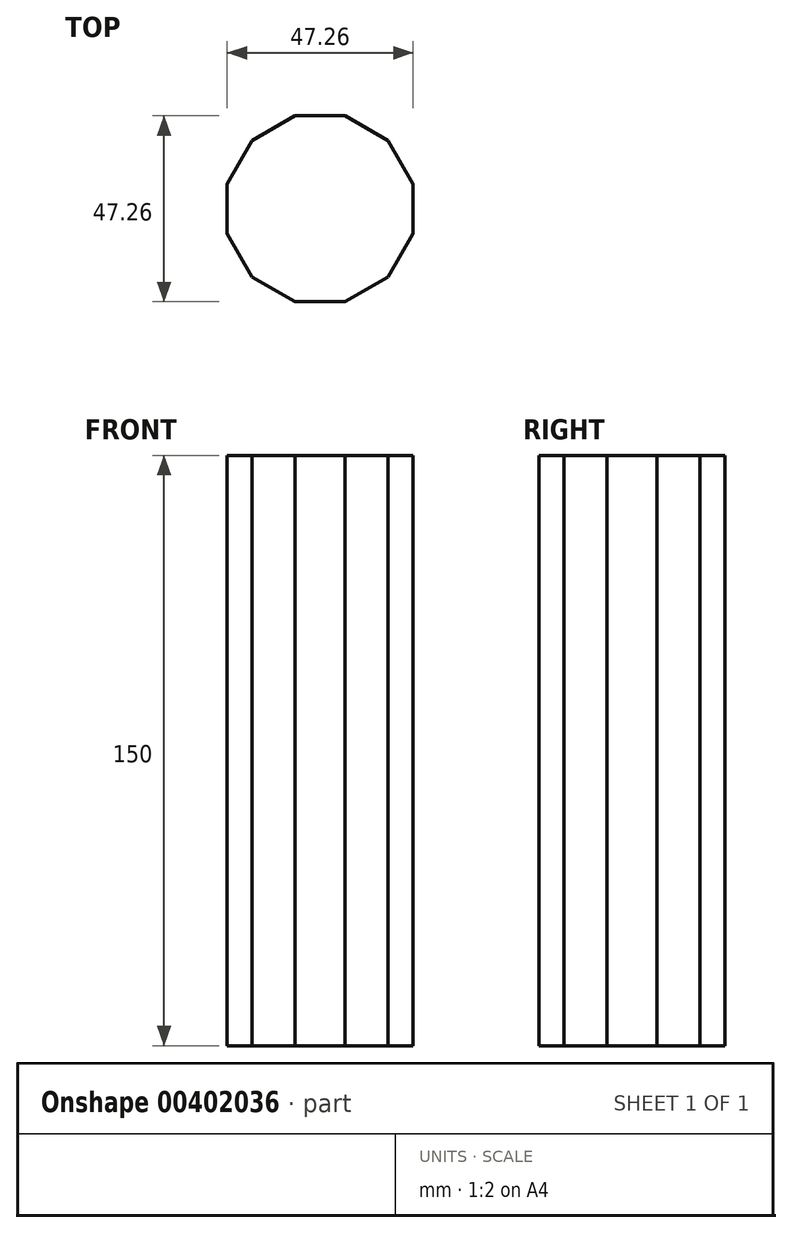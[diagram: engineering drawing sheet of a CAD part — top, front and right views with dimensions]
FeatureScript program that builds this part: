
annotation { "Feature Type Name" : "Feature", "Feature Type Description" : "" }
export const myFeature = defineFeature(function(context is Context, id is Id, definition is map)
    precondition{}
    {
        {
            var Q0;
            Q0=qCreatedBy(makeId("Top.planeOp"),FACE);
            var sketch = newSketch(context, id + "F0", { "sketchPlane" : qUnion([Q0])});
            skCircle(sketch, "E0.cCircle", {"center": v(0, 0) * mm, "radius": 23.63 * mm, "construction": true});
            skLineSegment(sketch, "E0.0", {"start": v(23.63, 6.33) * mm, "end": v(23.63, -6.33) * mm});
            skLineSegment(sketch, "E0.1", {"start": v(23.63, -6.33) * mm, "end": v(17.3, -17.3) * mm});
            skLineSegment(sketch, "E0.2", {"start": v(17.3, -17.3) * mm, "end": v(6.33, -23.63) * mm});
            skLineSegment(sketch, "E0.3", {"start": v(6.33, -23.63) * mm, "end": v(-6.33, -23.63) * mm});
            skLineSegment(sketch, "E0.4", {"start": v(-6.33, -23.63) * mm, "end": v(-17.3, -17.3) * mm});
            skLineSegment(sketch, "E0.5", {"start": v(-17.3, -17.3) * mm, "end": v(-23.63, -6.33) * mm});
            skLineSegment(sketch, "E0.6", {"start": v(-23.63, -6.33) * mm, "end": v(-23.63, 6.33) * mm});
            skLineSegment(sketch, "E0.7", {"start": v(-23.63, 6.33) * mm, "end": v(-17.3, 17.3) * mm});
            skLineSegment(sketch, "E0.8", {"start": v(-17.3, 17.3) * mm, "end": v(-6.33, 23.63) * mm});
            skLineSegment(sketch, "E0.9", {"start": v(-6.33, 23.63) * mm, "end": v(6.33, 23.63) * mm});
            skLineSegment(sketch, "E0.10", {"start": v(6.33, 23.63) * mm, "end": v(17.3, 17.3) * mm});
            skLineSegment(sketch, "E0.11", {"start": v(17.3, 17.3) * mm, "end": v(23.63, 6.33) * mm});
            skPoint(sketch, "E0.0.midPoint", {"position": v(23.63, 0) * mm});
            skSolve(sketch);
        }
        {
            var Q0;
            Q0 = qSketchRegion(id + "F0", true);
            extrude(context, id + "F1", {"entities" : qUnion([Q0]), "oppositeDirection" : true, "depth" : -150 * mm});
        }
    });
